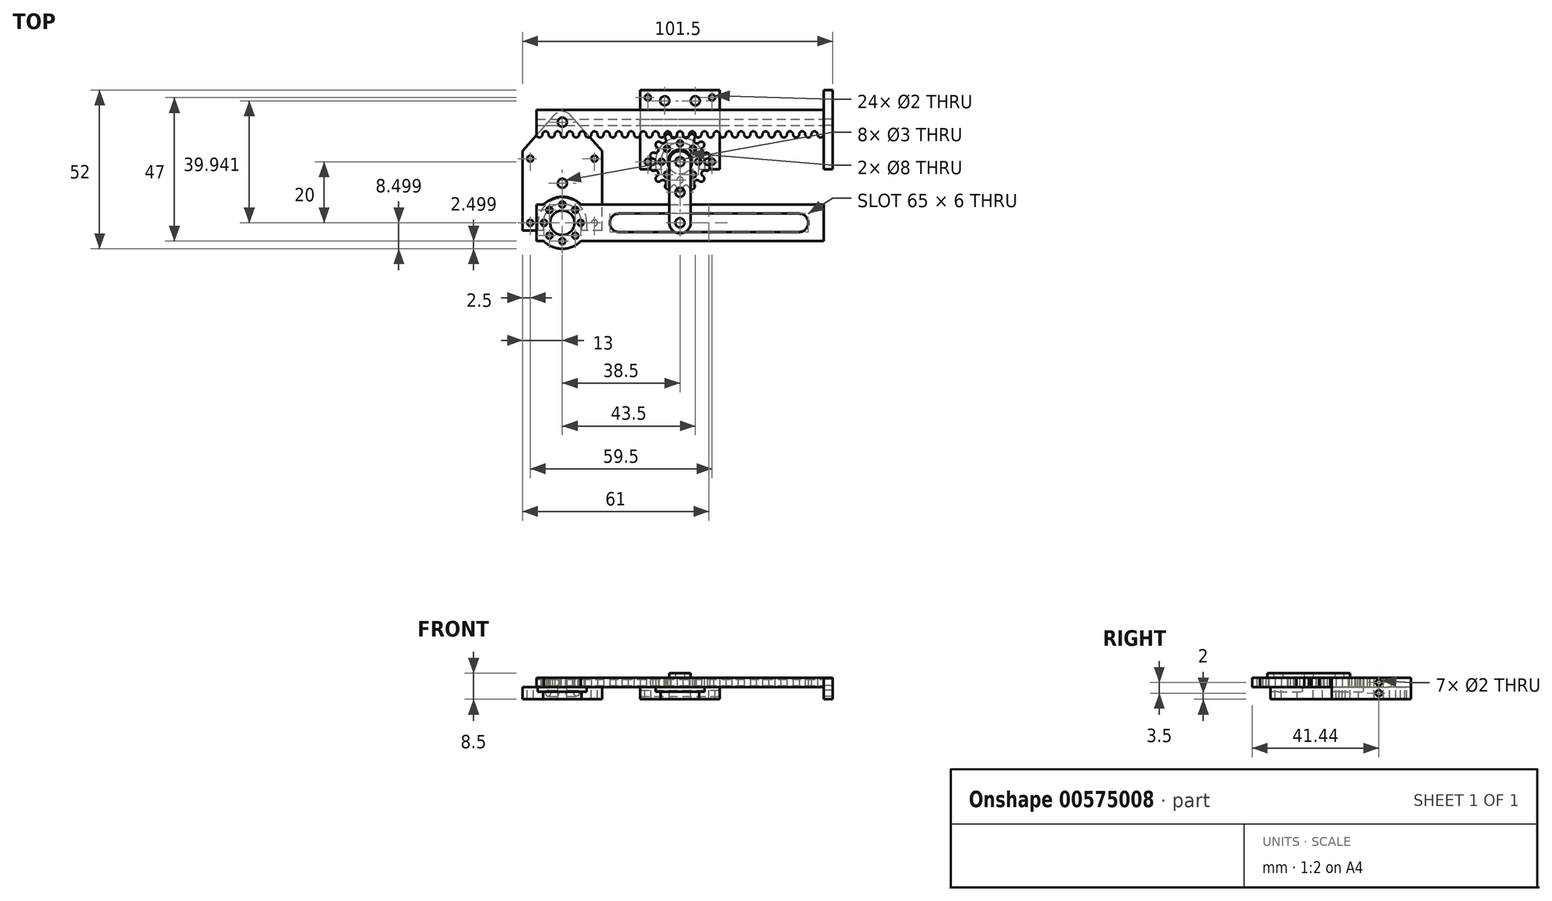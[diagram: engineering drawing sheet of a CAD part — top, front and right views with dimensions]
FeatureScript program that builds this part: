
annotation { "Feature Type Name" : "Feature", "Feature Type Description" : "" }
export const myFeature = defineFeature(function(context is Context, id is Id, definition is map)
    precondition{}
    {
        {
            var Q0;
            Q0=qCreatedBy(makeId("Top.planeOp"),FACE);
            var sketch = newSketch(context, id + "F0", { "sketchPlane" : qUnion([Q0])});
            skLineSegment(sketch, "E0.bottom", {"start": v(-25, 0) * mm, "end": v(13, 0) * mm, "construction": true});
            skLineSegment(sketch, "E0.top", {"start": v(-25, 8) * mm, "end": v(25, 8) * mm});
            skLineSegment(sketch, "E0.left", {"start": v(-25, 0) * mm, "end": v(-25, 8) * mm});
            skLineSegment(sketch, "E0.right", {"start": v(25, 0) * mm, "end": v(25, 8) * mm, "construction": true});
            skPoint(sketch, "E1", {"position": v(0, 0) * mm});
            skArc(sketch, "E2", {"start": v(-25, 0) * mm, "mid": v(-24, -1) * mm, "end": v(-23, 0) * mm});
            skArc(sketch, "E3.1.0.0", {"start": v(-21, 0) * mm, "mid": v(-22, 1) * mm, "end": v(-23, 0) * mm});
            skArc(sketch, "E3.2.0.0", {"start": v(-21, 0) * mm, "mid": v(-20, -1) * mm, "end": v(-19, 0) * mm});
            skArc(sketch, "E3.3.0.0", {"start": v(-17, 0) * mm, "mid": v(-18, 1) * mm, "end": v(-19, 0) * mm});
            skArc(sketch, "E3.4.0.0", {"start": v(-17, 0) * mm, "mid": v(-16, -1) * mm, "end": v(-15, 0) * mm});
            skArc(sketch, "E3.5.0.0", {"start": v(-13, 0) * mm, "mid": v(-14, 1) * mm, "end": v(-15, 0) * mm});
            skArc(sketch, "E3.6.0.0", {"start": v(-13, 0) * mm, "mid": v(-12, -1) * mm, "end": v(-11, 0) * mm});
            skArc(sketch, "E3.7.0.0", {"start": v(-9, 0) * mm, "mid": v(-10, 1) * mm, "end": v(-11, 0) * mm});
            skArc(sketch, "E3.8.0.0", {"start": v(-9, 0) * mm, "mid": v(-8, -1) * mm, "end": v(-7, 0) * mm});
            skArc(sketch, "E3.9.0.0", {"start": v(-5, 0) * mm, "mid": v(-6, 1) * mm, "end": v(-7, 0) * mm});
            skArc(sketch, "E3.10.0.0", {"start": v(-5, 0) * mm, "mid": v(-4, -1) * mm, "end": v(-3, 0) * mm});
            skArc(sketch, "E3.11.0.0", {"start": v(-1, 0) * mm, "mid": v(-2, 1) * mm, "end": v(-3, 0) * mm});
            skArc(sketch, "E3.12.0.0", {"start": v(-1, 0) * mm, "mid": v(0, -1) * mm, "end": v(1, 0) * mm});
            skArc(sketch, "E3.13.0.0", {"start": v(3, 0) * mm, "mid": v(2, 1) * mm, "end": v(1, 0) * mm});
            skArc(sketch, "E3.14.0.0", {"start": v(3, 0) * mm, "mid": v(4, -1) * mm, "end": v(5, 0) * mm});
            skArc(sketch, "E3.15.0.0", {"start": v(7, 0) * mm, "mid": v(6, 1) * mm, "end": v(5, 0) * mm});
            skArc(sketch, "E3.16.0.0", {"start": v(7, 0) * mm, "mid": v(8, -1) * mm, "end": v(9, 0) * mm});
            skArc(sketch, "E3.17.0.0", {"start": v(11, 0) * mm, "mid": v(10, 1) * mm, "end": v(9, 0) * mm});
            skArc(sketch, "E3.18.0.0", {"start": v(11, 0) * mm, "mid": v(12, -1) * mm, "end": v(13, 0) * mm});
            skArc(sketch, "E3.19.0.0", {"start": v(15, 0) * mm, "mid": v(14, 1) * mm, "end": v(13, 0) * mm});
            skLineSegment(sketch, "E3.direction1", {"start": v(-24, 0) * mm, "end": v(-22, 0) * mm, "construction": true});
            skArc(sketch, "E4.0.20.0", {"start": v(15, 0) * mm, "mid": v(16, -1) * mm, "end": v(17, 0) * mm});
            skArc(sketch, "E4.0.21.0", {"start": v(19, 0) * mm, "mid": v(18, 1) * mm, "end": v(17, 0) * mm});
            skArc(sketch, "E4.0.22.0", {"start": v(19, 0) * mm, "mid": v(20, -1) * mm, "end": v(21, 0) * mm});
            skArc(sketch, "E4.0.23.0", {"start": v(23, 0) * mm, "mid": v(22, 1) * mm, "end": v(21, 0) * mm});
            skArc(sketch, "E4.0.24.0", {"start": v(23, 0) * mm, "mid": v(24, -1) * mm, "end": v(25, 0) * mm});
            skLineSegment(sketch, "E5.trimOffspring", {"start": v(14, 0) * mm, "end": v(25, 0) * mm, "construction": true});
            skArc(sketch, "E6", {"start": v(27, 0) * mm, "mid": v(26, 1) * mm, "end": v(25, 0) * mm});
            skArc(sketch, "E7.1.0.0", {"start": v(27, 0) * mm, "mid": v(28, -1) * mm, "end": v(29, 0) * mm});
            skArc(sketch, "E7.2.0.0", {"start": v(31, 0) * mm, "mid": v(30, 1) * mm, "end": v(29, 0) * mm});
            skArc(sketch, "E7.3.0.0", {"start": v(31, 0) * mm, "mid": v(32, -1) * mm, "end": v(33, 0) * mm});
            skArc(sketch, "E7.4.0.0", {"start": v(35, 0) * mm, "mid": v(34, 1) * mm, "end": v(33, 0) * mm});
            skArc(sketch, "E7.5.0.0", {"start": v(35, 0) * mm, "mid": v(36, -1) * mm, "end": v(37, 0) * mm});
            skArc(sketch, "E7.6.0.0", {"start": v(39, 0) * mm, "mid": v(38, 1) * mm, "end": v(37, 0) * mm});
            skArc(sketch, "E7.7.0.0", {"start": v(39, 0) * mm, "mid": v(40, -1) * mm, "end": v(41, 0) * mm});
            skArc(sketch, "E7.8.0.0", {"start": v(43, 0) * mm, "mid": v(42, 1) * mm, "end": v(41, 0) * mm});
            skArc(sketch, "E7.9.0.0", {"start": v(43, 0) * mm, "mid": v(44, -1) * mm, "end": v(45, 0) * mm});
            skLineSegment(sketch, "E7.direction1", {"start": v(26, 0) * mm, "end": v(28, 0) * mm, "construction": true});
            skArc(sketch, "E8.0.10.0", {"start": v(47, 0) * mm, "mid": v(46, 1) * mm, "end": v(45, 0) * mm});
            skArc(sketch, "E8.0.11.0", {"start": v(47, 0) * mm, "mid": v(48, -1) * mm, "end": v(49, 0) * mm});
            skArc(sketch, "E8.0.12.0", {"start": v(51, 0) * mm, "mid": v(50, 1) * mm, "end": v(49, 0) * mm});
            skArc(sketch, "E8.0.13.0", {"start": v(51, 0) * mm, "mid": v(52, -1) * mm, "end": v(53, 0) * mm});
            skArc(sketch, "E8.0.14.0", {"start": v(55, 0) * mm, "mid": v(54, 1) * mm, "end": v(53, 0) * mm});
            skArc(sketch, "E8.0.15.0", {"start": v(55, 0) * mm, "mid": v(56, -1) * mm, "end": v(57, 0) * mm});
            skLineSegment(sketch, "E9", {"start": v(25, 8) * mm, "end": v(57, 8) * mm});
            skLineSegment(sketch, "E10", {"start": v(57, 8) * mm, "end": v(57, 0) * mm, "construction": true});
            skArc(sketch, "E11", {"start": v(59, 0) * mm, "mid": v(58, 1) * mm, "end": v(57, 0) * mm});
            skLineSegment(sketch, "E12", {"start": v(57, 8) * mm, "end": v(69, 8) * mm});
            skLineSegment(sketch, "E13", {"start": v(69, 8) * mm, "end": v(69, 0) * mm});
            skArc(sketch, "E14.1.0.0", {"start": v(59, 0) * mm, "mid": v(60, -1) * mm, "end": v(61, 0) * mm});
            skArc(sketch, "E14.2.0.0", {"start": v(63, 0) * mm, "mid": v(62, 1) * mm, "end": v(61, 0) * mm});
            skArc(sketch, "E14.3.0.0", {"start": v(63, 0) * mm, "mid": v(64, -1) * mm, "end": v(65, 0) * mm});
            skArc(sketch, "E14.4.0.0", {"start": v(67, 0) * mm, "mid": v(66, 1) * mm, "end": v(65, 0) * mm});
            skArc(sketch, "E14.5.0.0", {"start": v(67, 0) * mm, "mid": v(68, -1) * mm, "end": v(69, 0) * mm});
            skLineSegment(sketch, "E14.direction1", {"start": v(58, 0) * mm, "end": v(60, 0) * mm, "construction": true});
            skSolve(sketch);
        }
        {
            var Q0;
            Q0 = qSketchRegion(id + "F0", true);
            extrude(context, id + "F1", {"entities" : qUnion([Q0]), "depth" : 3 * mm, "offsetDistance" : 25 * mm});
        }
        {
            var Q0;
            Q0=qCreatedBy(makeId("Top.planeOp"),FACE);
            var sketch = newSketch(context, id + "F2", { "sketchPlane" : qUnion([Q0])});
            skArc(sketch, "E15.0", {"start": v(23, 0) * mm, "mid": v(22, 1) * mm, "end": v(21, 0) * mm, "construction": true});
            skArc(sketch, "E16", {"start": v(23, -0.12) * mm, "mid": v(22, 1) * mm, "end": v(21, -0.12) * mm});
            skCircle(sketch, "E17", {"center": v(22, -2.94) * mm, "radius": 1 * mm});
            skCircle(sketch, "E18", {"center": v(22, -8.94) * mm, "radius": 4 * mm});
            skPoint(sketch, "E19", {"position": v(22, -1) * mm});
            skCircle(sketch, "E20.1.0", {"center": v(17.76, -4.7) * mm, "radius": 1 * mm});
            skCircle(sketch, "E20.2.0", {"center": v(16, -8.94) * mm, "radius": 1 * mm});
            skCircle(sketch, "E21.1.3.0", {"center": v(17.76, -13.18) * mm, "radius": 1 * mm});
            skCircle(sketch, "E21.1.4.0", {"center": v(22, -14.94) * mm, "radius": 1 * mm});
            skCircle(sketch, "E21.1.5.0", {"center": v(26.24, -13.18) * mm, "radius": 1 * mm});
            skCircle(sketch, "E21.1.6.0", {"center": v(28, -8.94) * mm, "radius": 1 * mm});
            skCircle(sketch, "E21.1.7.0", {"center": v(26.24, -4.7) * mm, "radius": 1 * mm});
            skArc(sketch, "E22.1.0", {"start": v(19.07, -0.56) * mm, "mid": v(20.24, -1.2) * mm, "end": v(21, -0.12) * mm});
            skArc(sketch, "E22.2.0", {"start": v(19.07, -0.56) * mm, "mid": v(17.7, 0) * mm, "end": v(17.28, -1.43) * mm});
            skArc(sketch, "E23.1.3.0", {"start": v(15.72, -2.67) * mm, "mid": v(17.05, -2.74) * mm, "end": v(17.28, -1.43) * mm});
            skArc(sketch, "E23.1.4.0", {"start": v(15.72, -2.67) * mm, "mid": v(14.24, -2.75) * mm, "end": v(14.49, -4.22) * mm});
            skArc(sketch, "E23.1.5.0", {"start": v(13.62, -6.01) * mm, "mid": v(14.85, -5.5) * mm, "end": v(14.49, -4.22) * mm});
            skArc(sketch, "E23.1.6.0", {"start": v(13.62, -6.01) * mm, "mid": v(12.32, -6.73) * mm, "end": v(13.18, -7.95) * mm});
            skArc(sketch, "E23.1.7.0", {"start": v(13.18, -9.94) * mm, "mid": v(14.07, -8.94) * mm, "end": v(13.18, -7.95) * mm});
            skArc(sketch, "E23.1.8.0", {"start": v(13.18, -9.94) * mm, "mid": v(12.32, -11.15) * mm, "end": v(13.62, -11.87) * mm});
            skArc(sketch, "E23.1.9.0", {"start": v(14.49, -13.66) * mm, "mid": v(14.85, -12.38) * mm, "end": v(13.62, -11.87) * mm});
            skArc(sketch, "E23.1.10.0", {"start": v(14.49, -13.66) * mm, "mid": v(14.24, -15.13) * mm, "end": v(15.72, -15.22) * mm});
            skArc(sketch, "E23.1.11.0", {"start": v(17.28, -16.46) * mm, "mid": v(17.05, -15.14) * mm, "end": v(15.72, -15.22) * mm});
            skArc(sketch, "E23.1.12.0", {"start": v(17.28, -16.46) * mm, "mid": v(17.7, -17.89) * mm, "end": v(19.07, -17.32) * mm});
            skArc(sketch, "E23.1.13.0", {"start": v(21, -17.76) * mm, "mid": v(20.24, -16.67) * mm, "end": v(19.07, -17.32) * mm});
            skArc(sketch, "E23.1.14.0", {"start": v(21, -17.76) * mm, "mid": v(22, -18.87) * mm, "end": v(23, -17.76) * mm});
            skArc(sketch, "E23.1.15.0", {"start": v(24.93, -17.32) * mm, "mid": v(23.76, -16.67) * mm, "end": v(23, -17.76) * mm});
            skArc(sketch, "E23.1.16.0", {"start": v(24.93, -17.32) * mm, "mid": v(26.3, -17.89) * mm, "end": v(26.72, -16.46) * mm});
            skArc(sketch, "E23.1.17.0", {"start": v(28.28, -15.22) * mm, "mid": v(26.95, -15.14) * mm, "end": v(26.72, -16.46) * mm});
            skArc(sketch, "E23.1.18.0", {"start": v(28.28, -15.22) * mm, "mid": v(29.76, -15.13) * mm, "end": v(29.51, -13.66) * mm});
            skArc(sketch, "E23.1.19.0", {"start": v(30.38, -11.87) * mm, "mid": v(29.15, -12.38) * mm, "end": v(29.51, -13.66) * mm});
            skArc(sketch, "E24.1.20.0", {"start": v(30.38, -11.87) * mm, "mid": v(31.68, -11.15) * mm, "end": v(30.82, -9.94) * mm});
            skArc(sketch, "E24.1.21.0", {"start": v(30.82, -7.95) * mm, "mid": v(29.93, -8.94) * mm, "end": v(30.82, -9.94) * mm});
            skArc(sketch, "E25.1.22.0", {"start": v(30.82, -7.95) * mm, "mid": v(31.68, -6.73) * mm, "end": v(30.38, -6.01) * mm});
            skArc(sketch, "E25.1.23.0", {"start": v(29.51, -4.22) * mm, "mid": v(29.15, -5.5) * mm, "end": v(30.38, -6.01) * mm});
            skArc(sketch, "E26.1.24.0", {"start": v(29.51, -4.22) * mm, "mid": v(29.76, -2.75) * mm, "end": v(28.28, -2.67) * mm});
            skArc(sketch, "E26.1.25.0", {"start": v(26.72, -1.43) * mm, "mid": v(26.95, -2.74) * mm, "end": v(28.28, -2.67) * mm});
            skArc(sketch, "E27.1.26.0", {"start": v(26.72, -1.43) * mm, "mid": v(26.3, 0) * mm, "end": v(24.93, -0.56) * mm});
            skArc(sketch, "E27.1.27.0", {"start": v(23, -0.12) * mm, "mid": v(23.76, -1.2) * mm, "end": v(24.93, -0.56) * mm});
            skSolve(sketch);
        }
        {
            var Q0;
            Q0 = qSketchRegion(id + "F2", true);
            extrude(context, id + "F3", {"entities" : qUnion([Q0]), "depth" : 3 * mm, "offsetDistance" : 25 * mm});
        }
        {
            var Q0;
            Q0=qCreatedBy(makeId("Top.planeOp"),FACE);
            var sketch = newSketch(context, id + "F4", { "sketchPlane" : qUnion([Q0])});
            skCircle(sketch, "E28.0", {"center": v(22, -8.94) * mm, "radius": 4 * mm, "construction": true});
            skArc(sketch, "E29", {"start": v(28.25, -8.94) * mm, "mid": v(22, -2.7) * mm, "end": v(15.75, -8.94) * mm});
            skCircle(sketch, "E30", {"center": v(32.5, -8.94) * mm, "radius": 1 * mm});
            skLineSegment(sketch, "E31", {"start": v(22, -8.94) * mm, "end": v(22, 12.06) * mm, "construction": true});
            skCircle(sketch, "E32", {"center": v(32.5, 12.06) * mm, "radius": 1 * mm});
            skCircle(sketch, "E33.MirrorC", {"center": v(11.5, 12.06) * mm, "radius": 1 * mm});
            skCircle(sketch, "E34.MirrorC", {"center": v(11.5, -8.94) * mm, "radius": 1 * mm});
            skCircle(sketch, "E35", {"center": v(22, 11) * mm, "radius": 3 * mm, "construction": true});
            skCircle(sketch, "E36", {"center": v(22, 11) * mm, "radius": 1.5 * mm});
            skLineSegment(sketch, "E37.bottom", {"start": v(9, 14.56) * mm, "end": v(35, 14.56) * mm});
            skLineSegment(sketch, "E37.top", {"start": v(9, -11.44) * mm, "end": v(15.75, -11.44) * mm});
            skLineSegment(sketch, "E37.left", {"start": v(9, 14.56) * mm, "end": v(9, -11.44) * mm});
            skLineSegment(sketch, "E37.right", {"start": v(35, 14.56) * mm, "end": v(35, -11.44) * mm});
            skPoint(sketch, "E37.middle", {"position": v(22, 1.56) * mm});
            skLineSegment(sketch, "E38", {"start": v(15.75, -8.94) * mm, "end": v(15.75, -11.44) * mm});
            skLineSegment(sketch, "E39.MirrorCS", {"start": v(28.25, -8.94) * mm, "end": v(28.25, -11.44) * mm});
            skLineSegment(sketch, "E40.trimOffspring", {"start": v(28.25, -11.44) * mm, "end": v(35, -11.44) * mm});
            skCircle(sketch, "E41", {"center": v(27, 11) * mm, "radius": 1.5 * mm});
            skCircle(sketch, "E42", {"center": v(27, 11) * mm, "radius": 3 * mm, "construction": true});
            skCircle(sketch, "E43.MirrorC", {"center": v(17, 11) * mm, "radius": 1.5 * mm});
            skCircle(sketch, "E44.MirrorC", {"center": v(17, 11) * mm, "radius": 3 * mm, "construction": true});
            skSolve(sketch);
        }
        {
            var Q0;
            Q0 = qSketchRegion(id + "F4", true);
            var Q1;
            Q1=makeQuery(id+"F4.imprint","IMPRINT",FACE,{"disambiguationData":[TD([[makeQuery(id+"F4.imprint","IMPRINT",EDGE,{"derivedFrom":sQuery(id+"F4.wireOp",EDGE,"E36")}),1.0]])]});
            extrude(context, id + "F5", {"entities" : qUnion([Q0, Q1]), "oppositeDirection" : true, "depth" : 4 * mm, "offsetDistance" : 25 * mm});
        }
        {
            var Q0;
            Q0=makeQuery(id+"F5.opExtrude","CAP_FACE",FACE,{"disambiguationData":[OSD([sQuery(id+"F4.wireOp",EDGE,"E29"),sQuery(id+"F4.wireOp",EDGE,"E30"),sQuery(id+"F4.wireOp",EDGE,"E32"),sQuery(id+"F4.wireOp",EDGE,"E33.MirrorC"),sQuery(id+"F4.wireOp",EDGE,"E34.MirrorC"),sQuery(id+"F4.wireOp",EDGE,"E36"),sQuery(id+"F4.wireOp",EDGE,"E37.bottom"),sQuery(id+"F4.wireOp",EDGE,"E37.top"),sQuery(id+"F4.wireOp",EDGE,"E37.left"),sQuery(id+"F4.wireOp",EDGE,"E37.right"),sQuery(id+"F4.wireOp",EDGE,"E38"),sQuery(id+"F4.wireOp",EDGE,"E39.MirrorCS"),sQuery(id+"F4.wireOp",EDGE,"E40.trimOffspring")])],"isStart":true});
            var sketch = newSketch(context, id + "F6", { "sketchPlane" : qUnion([Q0])});
            skArc(sketch, "E45.0", {"start": v(28.25, -8.94) * mm, "mid": v(22, -2.7) * mm, "end": v(15.75, -8.94) * mm});
            skArc(sketch, "E46", {"start": v(30, -8.94) * mm, "mid": v(22, -0.94) * mm, "end": v(14, -8.94) * mm});
            skLineSegment(sketch, "E47", {"start": v(14, -8.94) * mm, "end": v(14, -11.44) * mm});
            skLineSegment(sketch, "E48", {"start": v(14, -11.44) * mm, "end": v(15.75, -11.44) * mm});
            skLineSegment(sketch, "E49", {"start": v(15.75, -11.44) * mm, "end": v(15.75, -8.94) * mm});
            skLineSegment(sketch, "E50", {"start": v(22, -8.94) * mm, "end": v(22, -11.44) * mm, "construction": true});
            skArc(sketch, "E51.MirrorCS", {"start": v(15.75, -8.94) * mm, "mid": v(22, -2.7) * mm, "end": v(28.25, -8.94) * mm});
            skLineSegment(sketch, "E52.MirrorCS", {"start": v(28.25, -11.44) * mm, "end": v(28.25, -8.94) * mm});
            skLineSegment(sketch, "E53.MirrorCS", {"start": v(30, -11.44) * mm, "end": v(28.25, -11.44) * mm});
            skLineSegment(sketch, "E54.MirrorCS", {"start": v(30, -8.94) * mm, "end": v(30, -11.44) * mm});
            skSolve(sketch);
        }
        {
            var Q0;
            Q0 = qSketchRegion(id + "F6", true);
            extrude(context, id + "F7", {"entities" : qUnion([Q0]), "operationType" : NewBodyOperationType.REMOVE, "oppositeDirection" : true, "depth" : 1.5 * mm, "offsetDistance" : 25 * mm});
        }
        {
            var Q0;
            Q0=qCreatedBy(makeId("Top.planeOp"),FACE);
            var sketch = newSketch(context, id + "F8", { "sketchPlane" : qUnion([Q0])});
            skPoint(sketch, "E55.0", {"position": v(-25, 8) * mm});
            skLineSegment(sketch, "E56.bottom", {"start": v(-25, -22.94) * mm, "end": v(69, -22.94) * mm});
            skLineSegment(sketch, "E56.top", {"start": v(-25, -34.94) * mm, "end": v(69, -34.94) * mm});
            skLineSegment(sketch, "E56.left", {"start": v(-25, -22.94) * mm, "end": v(-25, -34.94) * mm});
            skLineSegment(sketch, "E56.right", {"start": v(69, -22.94) * mm, "end": v(69, -34.94) * mm});
            skCircle(sketch, "E57", {"center": v(61, -28.94) * mm, "radius": 3 * mm});
            skPoint(sketch, "E57.centerSnap0", {"position": v(69, -28.94) * mm});
            skCircle(sketch, "E58", {"center": v(-16.5, -28.94) * mm, "radius": 4 * mm});
            skCircle(sketch, "E59", {"center": v(-10.5, -28.94) * mm, "radius": 1 * mm});
            skCircle(sketch, "E60.1.0", {"center": v(-12.26, -24.7) * mm, "radius": 1 * mm});
            skCircle(sketch, "E60.2.0", {"center": v(-16.5, -22.94) * mm, "radius": 1 * mm});
            skCircle(sketch, "E61.1.3.0", {"center": v(-20.74, -24.7) * mm, "radius": 1 * mm});
            skCircle(sketch, "E61.1.4.0", {"center": v(-22.5, -28.94) * mm, "radius": 1 * mm});
            skCircle(sketch, "E61.1.5.0", {"center": v(-20.74, -33.18) * mm, "radius": 1 * mm});
            skCircle(sketch, "E61.1.6.0", {"center": v(-16.5, -34.94) * mm, "radius": 1 * mm});
            skCircle(sketch, "E61.1.7.0", {"center": v(-12.26, -33.18) * mm, "radius": 1 * mm});
            skArc(sketch, "E62", {"start": v(-10.48, -22.94) * mm, "mid": v(-16.5, -20.44) * mm, "end": v(-22.52, -22.94) * mm});
            skPoint(sketch, "E63", {"position": v(-16.5, -20.44) * mm});
            skLineSegment(sketch, "E64", {"start": v(-22.5, -28.94) * mm, "end": v(-10.5, -28.94) * mm, "construction": true});
            skArc(sketch, "E65.MirrorCS", {"start": v(-10.48, -34.94) * mm, "mid": v(-16.5, -37.44) * mm, "end": v(-22.52, -34.94) * mm});
            skCircle(sketch, "E66", {"center": v(2, -28.94) * mm, "radius": 3 * mm});
            skLineSegment(sketch, "E67", {"start": v(61, -25.94) * mm, "end": v(2, -25.94) * mm});
            skLineSegment(sketch, "E68.MirrorCS", {"start": v(61, -31.94) * mm, "end": v(2, -31.94) * mm});
            skCircle(sketch, "E69.0", {"center": v(22, -8.94) * mm, "radius": 4 * mm, "construction": true});
            skPoint(sketch, "E70", {"position": v(-1, -28.94) * mm});
            skPoint(sketch, "E71.0", {"position": v(69, 8) * mm});
            skSolve(sketch);
        }
        {
            var Q0;
            Q0 = qSketchRegion(id + "F8", true);
            extrude(context, id + "F9", {"entities" : qUnion([Q0]), "depth" : 3 * mm, "offsetDistance" : 25 * mm});
        }
        {
            var Q0;
            Q0=makeQuery(id+"F3.opExtrude","CAP_FACE",FACE,{"disambiguationData":[OSD([sQuery(id+"F2.wireOp",EDGE,"E16"),sQuery(id+"F2.wireOp",EDGE,"E17"),sQuery(id+"F2.wireOp",EDGE,"E18"),sQuery(id+"F2.wireOp",EDGE,"E20.1.0"),sQuery(id+"F2.wireOp",EDGE,"E20.2.0"),sQuery(id+"F2.wireOp",EDGE,"E21.1.3.0"),sQuery(id+"F2.wireOp",EDGE,"E21.1.4.0"),sQuery(id+"F2.wireOp",EDGE,"E21.1.5.0"),sQuery(id+"F2.wireOp",EDGE,"E21.1.6.0"),sQuery(id+"F2.wireOp",EDGE,"E21.1.7.0"),sQuery(id+"F2.wireOp",EDGE,"E22.1.0"),sQuery(id+"F2.wireOp",EDGE,"E22.2.0"),sQuery(id+"F2.wireOp",EDGE,"E23.1.3.0"),sQuery(id+"F2.wireOp",EDGE,"E23.1.4.0"),sQuery(id+"F2.wireOp",EDGE,"E23.1.5.0"),sQuery(id+"F2.wireOp",EDGE,"E23.1.6.0"),sQuery(id+"F2.wireOp",EDGE,"E23.1.7.0"),sQuery(id+"F2.wireOp",EDGE,"E23.1.8.0"),sQuery(id+"F2.wireOp",EDGE,"E23.1.9.0"),sQuery(id+"F2.wireOp",EDGE,"E23.1.10.0"),sQuery(id+"F2.wireOp",EDGE,"E23.1.11.0"),sQuery(id+"F2.wireOp",EDGE,"E23.1.12.0"),sQuery(id+"F2.wireOp",EDGE,"E23.1.13.0"),sQuery(id+"F2.wireOp",EDGE,"E23.1.14.0"),sQuery(id+"F2.wireOp",EDGE,"E23.1.15.0"),sQuery(id+"F2.wireOp",EDGE,"E23.1.16.0"),sQuery(id+"F2.wireOp",EDGE,"E23.1.17.0"),sQuery(id+"F2.wireOp",EDGE,"E23.1.18.0"),sQuery(id+"F2.wireOp",EDGE,"E23.1.19.0"),sQuery(id+"F2.wireOp",EDGE,"E24.1.20.0"),sQuery(id+"F2.wireOp",EDGE,"E24.1.21.0"),sQuery(id+"F2.wireOp",EDGE,"E25.1.22.0"),sQuery(id+"F2.wireOp",EDGE,"E25.1.23.0"),sQuery(id+"F2.wireOp",EDGE,"E26.1.24.0"),sQuery(id+"F2.wireOp",EDGE,"E26.1.25.0"),sQuery(id+"F2.wireOp",EDGE,"E27.1.26.0"),sQuery(id+"F2.wireOp",EDGE,"E27.1.27.0")])],"isStart":false});
            var sketch = newSketch(context, id + "F10", { "sketchPlane" : qUnion([Q0])});
            skCircle(sketch, "E72", {"center": v(22, -8.94) * mm, "radius": 1.5 * mm});
            skArc(sketch, "E73", {"start": v(25.5, -8.94) * mm, "mid": v(22, -5.44) * mm, "end": v(18.5, -8.94) * mm});
            skPoint(sketch, "E74.0", {"position": v(64, -28.94) * mm});
            skLineSegment(sketch, "E75", {"start": v(22, -8.94) * mm, "end": v(22, -28.94) * mm, "construction": true});
            skArc(sketch, "E76", {"start": v(18.5, -28.94) * mm, "mid": v(22, -32.44) * mm, "end": v(25.5, -28.94) * mm});
            skCircle(sketch, "E77", {"center": v(22, -28.94) * mm, "radius": 1.5 * mm});
            skLineSegment(sketch, "E78", {"start": v(25.5, -8.94) * mm, "end": v(25.5, -28.94) * mm});
            skLineSegment(sketch, "E79.MirrorCS", {"start": v(18.5, -8.94) * mm, "end": v(18.5, -28.94) * mm});
            skCircle(sketch, "E80", {"center": v(22, -18.94) * mm, "radius": 1.5 * mm});
            skSolve(sketch);
        }
        {
            var Q0;
            Q0 = qSketchRegion(id + "F10", true);
            extrude(context, id + "F11", {"entities" : qUnion([Q0]), "depth" : 1.5 * mm, "offsetDistance" : 25 * mm});
        }
        {
            var Q0;
            Q0=qCreatedBy(makeId("Top.planeOp"),FACE);
            var sketch = newSketch(context, id + "F12", { "sketchPlane" : qUnion([Q0])});
            skCircle(sketch, "E81.0", {"center": v(-16.5, -28.94) * mm, "radius": 4 * mm, "construction": true});
            skArc(sketch, "E82", {"start": v(-10.25, -28.94) * mm, "mid": v(-16.5, -22.7) * mm, "end": v(-22.75, -28.94) * mm});
            skCircle(sketch, "E83", {"center": v(-6, -28.94) * mm, "radius": 1 * mm});
            skLineSegment(sketch, "E84", {"start": v(-16.5, -28.94) * mm, "end": v(-16.5, -7.94) * mm, "construction": true});
            skCircle(sketch, "E85", {"center": v(-6, -7.94) * mm, "radius": 1 * mm});
            skCircle(sketch, "E86.MirrorC", {"center": v(-27, -7.94) * mm, "radius": 1 * mm});
            skCircle(sketch, "E87.MirrorC", {"center": v(-27, -28.94) * mm, "radius": 1 * mm});
            skLineSegment(sketch, "E88.bottom", {"start": v(-3.5, -31.44) * mm, "end": v(-10.25, -31.44) * mm});
            skLineSegment(sketch, "E88.top", {"start": v(-3.5, -5.44) * mm, "end": v(-29.5, -5.44) * mm});
            skLineSegment(sketch, "E88.left", {"start": v(-3.5, -31.44) * mm, "end": v(-3.5, -5.44) * mm});
            skLineSegment(sketch, "E88.right", {"start": v(-29.5, -31.44) * mm, "end": v(-29.5, -5.44) * mm});
            skPoint(sketch, "E88.middle", {"position": v(-16.5, -18.44) * mm});
            skCircle(sketch, "E89", {"center": v(-16.5, 4) * mm, "radius": 1.5 * mm});
            skPoint(sketch, "E90.0", {"position": v(-25, 4) * mm});
            skArc(sketch, "E91", {"start": v(-13.88, 6.32) * mm, "mid": v(-16.5, 7.5) * mm, "end": v(-19.12, 6.32) * mm});
            skLineSegment(sketch, "E92", {"start": v(-29.5, -5.44) * mm, "end": v(-19.12, 6.32) * mm});
            skLineSegment(sketch, "E93.MirrorCS", {"start": v(-3.5, -5.44) * mm, "end": v(-13.88, 6.32) * mm});
            skLineSegment(sketch, "E94", {"start": v(-10.25, -28.94) * mm, "end": v(-10.25, -31.44) * mm});
            skLineSegment(sketch, "E95.MirrorCS", {"start": v(-22.75, -28.94) * mm, "end": v(-22.75, -31.44) * mm});
            skLineSegment(sketch, "E96.trimOffspring", {"start": v(-22.75, -31.44) * mm, "end": v(-29.5, -31.44) * mm});
            skArc(sketch, "E97", {"start": v(-24.1, -31.44) * mm, "mid": v(-16.5, -36.94) * mm, "end": v(-8.9, -31.44) * mm, "construction": true});
            skLineSegment(sketch, "E98", {"start": v(-24.5, -28.94) * mm, "end": v(-24.5, -31.44) * mm});
            skLineSegment(sketch, "E99.MirrorCS", {"start": v(-8.5, -28.94) * mm, "end": v(-8.5, -31.44) * mm});
            skArc(sketch, "E100.trimOffspring", {"start": v(-8.5, -28.94) * mm, "mid": v(-16.5, -20.94) * mm, "end": v(-24.5, -28.94) * mm});
            skSolve(sketch);
        }
        {
            var Q0;
            Q0 = qSketchRegion(id + "F12", true);
            extrude(context, id + "F13", {"entities" : qUnion([Q0]), "oppositeDirection" : true, "depth" : 4 * mm, "offsetDistance" : 25 * mm});
        }
        {
            var Q0;
            Q0=makeQuery(id+"F12.imprint","IMPRINT",FACE,{"disambiguationData":[TD([[makeQuery(id+"F12.imprint","IMPRINT",EDGE,{"derivedFrom":sQuery(id+"F12.wireOp",EDGE,"E82")}),-1.0]])]});
            extrude(context, id + "F14", {"entities" : qUnion([Q0]), "operationType" : NewBodyOperationType.REMOVE, "oppositeDirection" : true, "depth" : 1.5 * mm, "offsetDistance" : 25 * mm});
        }
        {
            var Q0;
            Q0=makeQuery(id+"F1.opExtrude","CAP_FACE",FACE,{"disambiguationData":[OSD([sQuery(id+"F0.wireOp",EDGE,"E0.top"),sQuery(id+"F0.wireOp",EDGE,"E0.left"),sQuery(id+"F0.wireOp",EDGE,"E2"),sQuery(id+"F0.wireOp",EDGE,"E3.1.0.0"),sQuery(id+"F0.wireOp",EDGE,"E3.2.0.0"),sQuery(id+"F0.wireOp",EDGE,"E3.3.0.0"),sQuery(id+"F0.wireOp",EDGE,"E3.4.0.0"),sQuery(id+"F0.wireOp",EDGE,"E3.5.0.0"),sQuery(id+"F0.wireOp",EDGE,"E3.6.0.0"),sQuery(id+"F0.wireOp",EDGE,"E3.7.0.0"),sQuery(id+"F0.wireOp",EDGE,"E3.8.0.0"),sQuery(id+"F0.wireOp",EDGE,"E3.9.0.0"),sQuery(id+"F0.wireOp",EDGE,"E3.10.0.0"),sQuery(id+"F0.wireOp",EDGE,"E3.11.0.0"),sQuery(id+"F0.wireOp",EDGE,"E3.12.0.0"),sQuery(id+"F0.wireOp",EDGE,"E3.13.0.0"),sQuery(id+"F0.wireOp",EDGE,"E3.14.0.0"),sQuery(id+"F0.wireOp",EDGE,"E3.15.0.0"),sQuery(id+"F0.wireOp",EDGE,"E3.16.0.0"),sQuery(id+"F0.wireOp",EDGE,"E3.17.0.0"),sQuery(id+"F0.wireOp",EDGE,"E3.18.0.0"),sQuery(id+"F0.wireOp",EDGE,"E3.19.0.0"),sQuery(id+"F0.wireOp",EDGE,"E4.0.20.0"),sQuery(id+"F0.wireOp",EDGE,"E4.0.21.0"),sQuery(id+"F0.wireOp",EDGE,"E4.0.22.0"),sQuery(id+"F0.wireOp",EDGE,"E4.0.23.0"),sQuery(id+"F0.wireOp",EDGE,"E4.0.24.0"),sQuery(id+"F0.wireOp",EDGE,"E6"),sQuery(id+"F0.wireOp",EDGE,"E7.1.0.0"),sQuery(id+"F0.wireOp",EDGE,"E7.2.0.0"),sQuery(id+"F0.wireOp",EDGE,"E7.3.0.0"),sQuery(id+"F0.wireOp",EDGE,"E7.4.0.0"),sQuery(id+"F0.wireOp",EDGE,"E7.5.0.0"),sQuery(id+"F0.wireOp",EDGE,"E7.6.0.0"),sQuery(id+"F0.wireOp",EDGE,"E7.7.0.0"),sQuery(id+"F0.wireOp",EDGE,"E7.8.0.0"),sQuery(id+"F0.wireOp",EDGE,"E7.9.0.0"),sQuery(id+"F0.wireOp",EDGE,"E8.0.10.0"),sQuery(id+"F0.wireOp",EDGE,"E8.0.11.0"),sQuery(id+"F0.wireOp",EDGE,"E8.0.12.0"),sQuery(id+"F0.wireOp",EDGE,"E8.0.13.0"),sQuery(id+"F0.wireOp",EDGE,"E8.0.14.0"),sQuery(id+"F0.wireOp",EDGE,"E8.0.15.0"),sQuery(id+"F0.wireOp",EDGE,"E9"),sQuery(id+"F0.wireOp",EDGE,"E10")])],"isStart":false});
            var sketch = newSketch(context, id + "F15", { "sketchPlane" : qUnion([Q0])});
            skCircle(sketch, "E101.0", {"center": v(-16.5, 4) * mm, "radius": 1.5 * mm});
            skSolve(sketch);
        }
        {
            var Q0;
            Q0 = qSketchRegion(id + "F15", true);
            extrude(context, id + "F16", {"entities" : qUnion([Q0]), "operationType" : NewBodyOperationType.REMOVE, "endBound" : BoundingType.UP_TO_NEXT, "oppositeDirection" : true, "depth" : 25 * mm, "offsetDistance" : 25 * mm});
        }
        {
            var Q0;
            Q0=makeQuery(id+"F13.opExtrude","CAP_FACE",FACE,{"disambiguationData":[OSD([sQuery(id+"F12.wireOp",EDGE,"E82"),sQuery(id+"F12.wireOp",EDGE,"E83"),sQuery(id+"F12.wireOp",EDGE,"E85"),sQuery(id+"F12.wireOp",EDGE,"E86.MirrorC"),sQuery(id+"F12.wireOp",EDGE,"E87.MirrorC"),sQuery(id+"F12.wireOp",EDGE,"E88.bottom"),sQuery(id+"F12.wireOp",EDGE,"E88.left"),sQuery(id+"F12.wireOp",EDGE,"E88.right"),sQuery(id+"F12.wireOp",EDGE,"E89"),sQuery(id+"F12.wireOp",EDGE,"E91"),sQuery(id+"F12.wireOp",EDGE,"E92"),sQuery(id+"F12.wireOp",EDGE,"E93.MirrorCS"),sQuery(id+"F12.wireOp",EDGE,"E94"),sQuery(id+"F12.wireOp",EDGE,"E95.MirrorCS"),sQuery(id+"F12.wireOp",EDGE,"E96.trimOffspring")])],"isStart":true});
            var sketch = newSketch(context, id + "F17", { "sketchPlane" : qUnion([Q0])});
            skCircle(sketch, "E102.0", {"center": v(-16.5, 4) * mm, "radius": 1.5 * mm, "construction": true});
            skCircle(sketch, "E103.0", {"center": v(22, -8.94) * mm, "radius": 4 * mm, "construction": true});
            skCircle(sketch, "E104", {"center": v(-16.5, -16) * mm, "radius": 1.5 * mm});
            skCircle(sketch, "E105.0", {"center": v(-16.5, -28.94) * mm, "radius": 4 * mm, "construction": true});
            skSolve(sketch);
        }
        {
            var Q0;
            Q0 = qSketchRegion(id + "F17", true);
            extrude(context, id + "F18", {"entities" : qUnion([Q0]), "operationType" : NewBodyOperationType.REMOVE, "endBound" : BoundingType.UP_TO_NEXT, "oppositeDirection" : true, "depth" : 25 * mm, "offsetDistance" : 25 * mm});
        }
        {
            var Q0;
            Q0=makeQuery(id+"F1.opExtrude","SWEPT_FACE",FACE,{"disambiguationData":[OSD([sQuery(id+"F0.wireOp",EDGE,"E13")])]});
            var sketch = newSketch(context, id + "F19", { "sketchPlane" : qUnion([Q0])});
            skCircle(sketch, "E106", {"center": v(4, 1.5) * mm, "radius": 1 * mm});
            skPoint(sketch, "E106.centerSnap0", {"position": v(4, 0) * mm});
            skPoint(sketch, "E106.centerSnap1", {"position": v(8, 1.5) * mm});
            skPoint(sketch, "E107.0", {"position": v(14.56, -2) * mm});
            skCircle(sketch, "E108", {"center": v(4, -2) * mm, "radius": 1 * mm});
            skSolve(sketch);
        }
        {
            var Q0;
            Q0 = qSketchRegion(id + "F19", true);
            extrude(context, id + "F20", {"entities" : qUnion([Q0]), "operationType" : NewBodyOperationType.REMOVE, "endBound" : BoundingType.THROUGH_ALL, "oppositeDirection" : true, "depth" : 25 * mm, "offsetDistance" : 25 * mm});
        }
        {
            var Q0;
            Q0=makeQuery(id+"F1.opExtrude","SWEPT_FACE",FACE,{"disambiguationData":[OSD([sQuery(id+"F0.wireOp",EDGE,"E13")])]});
            var sketch = newSketch(context, id + "F21", { "sketchPlane" : qUnion([Q0])});
            skPoint(sketch, "E109.0", {"position": v(14.56, -4) * mm});
            skPoint(sketch, "E110.0", {"position": v(-11.44, -4) * mm});
            skPoint(sketch, "E111.0", {"position": v(8, 3) * mm});
            skLineSegment(sketch, "E112.bottom", {"start": v(-11.44, -4) * mm, "end": v(14.56, -4) * mm});
            skLineSegment(sketch, "E112.top", {"start": v(-11.44, 3) * mm, "end": v(14.56, 3) * mm});
            skLineSegment(sketch, "E112.left", {"start": v(-11.44, -4) * mm, "end": v(-11.44, 3) * mm});
            skLineSegment(sketch, "E112.right", {"start": v(14.56, -4) * mm, "end": v(14.56, 3) * mm});
            skCircle(sketch, "E113.0", {"center": v(4, 1.5) * mm, "radius": 1 * mm});
            skCircle(sketch, "E114.0", {"center": v(4, -2) * mm, "radius": 1 * mm});
            skSolve(sketch);
        }
        {
            var Q0;
            Q0 = qSketchRegion(id + "F21", true);
            extrude(context, id + "F22", {"entities" : qUnion([Q0]), "depth" : 3 * mm, "offsetDistance" : 25 * mm});
        }
    });
